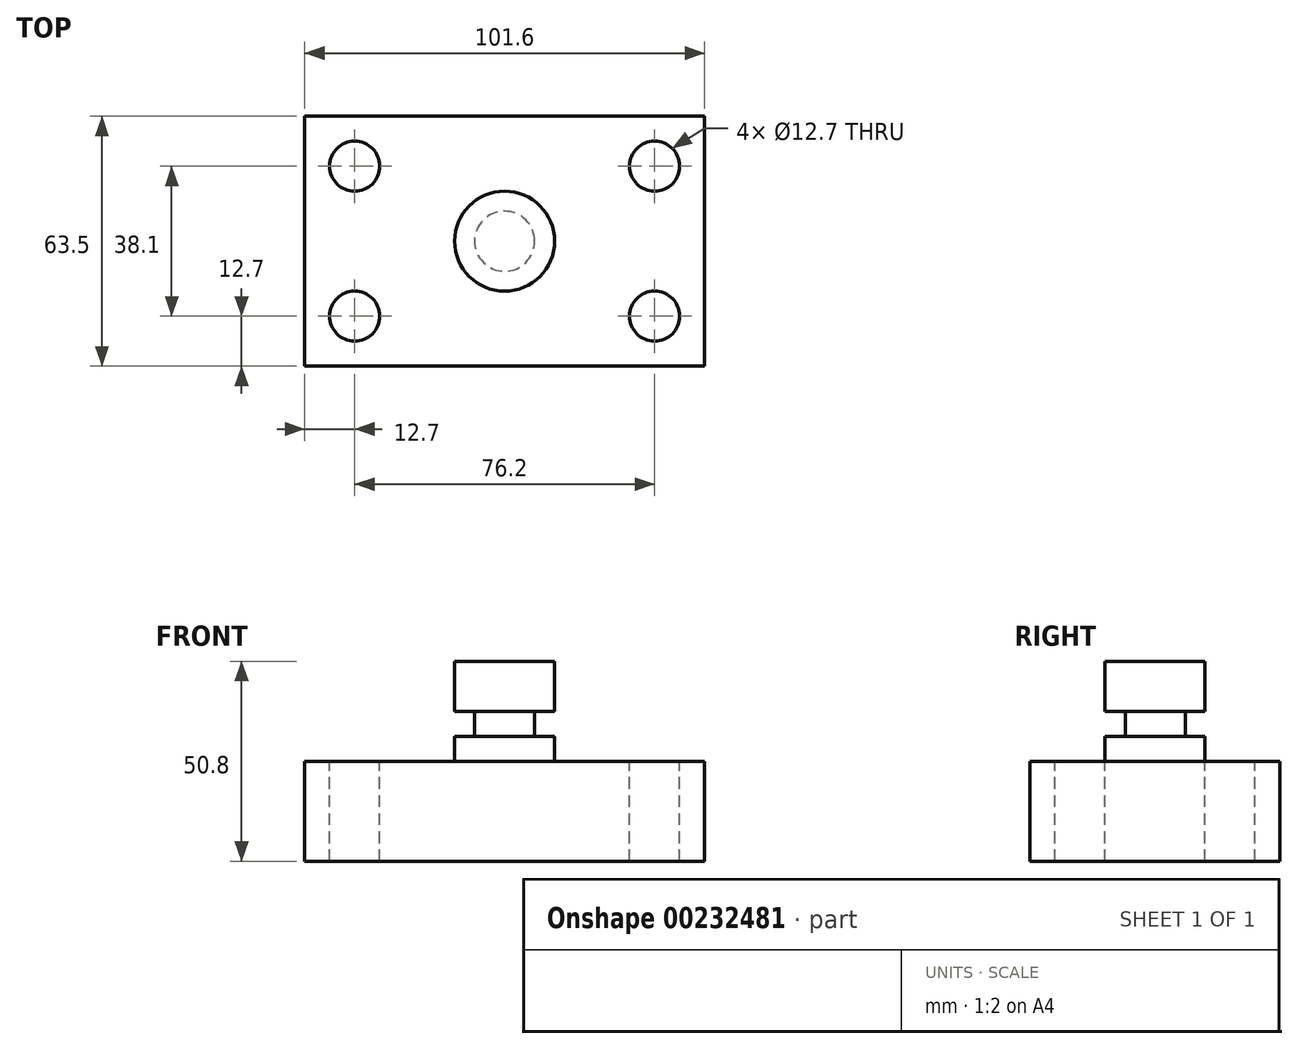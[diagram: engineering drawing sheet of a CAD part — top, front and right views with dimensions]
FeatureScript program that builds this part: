
annotation { "Feature Type Name" : "Feature", "Feature Type Description" : "" }
export const myFeature = defineFeature(function(context is Context, id is Id, definition is map)
    precondition{}
    {
        {
            var Q0;
            Q0=qCreatedBy(makeId("Top.planeOp"),FACE);
            var sketch = newSketch(context, id + "F0", { "sketchPlane" : qUnion([Q0])});
            skLineSegment(sketch, "E0.bottom", {"start": v(-50.8, 31.75) * mm, "end": v(50.8, 31.75) * mm});
            skLineSegment(sketch, "E0.top", {"start": v(-50.8, -31.75) * mm, "end": v(50.8, -31.75) * mm});
            skLineSegment(sketch, "E0.left", {"start": v(-50.8, 31.75) * mm, "end": v(-50.8, -31.75) * mm});
            skLineSegment(sketch, "E0.right", {"start": v(50.8, 31.75) * mm, "end": v(50.8, -31.75) * mm});
            skPoint(sketch, "E0.middle", {"position": v(0, 0) * mm});
            skSolve(sketch);
        }
        {
            var Q0;
            Q0=makeQuery(id+"F0.imprint","IMPRINT",FACE,{"disambiguationData":[TD([[makeQuery(id+"F0.imprint","IMPRINT",EDGE,{"derivedFrom":sQuery(id+"F0.wireOp",EDGE,"E0.bottom")}),-1.0]])]});
            extrude(context, id + "F1", {"entities" : qUnion([Q0]), "flatOperationType" : FlatOperationType.REMOVE, "offsetDistance" : 25.4 * mm, "depth" : 25.4 * mm, "domain" : OperationDomain.MODEL});
        }
        {
            var Q0;
            Q0=makeQuery(id+"F1.opExtrude","CAP_FACE",FACE,{"disambiguationData":[OSD([sQuery(id+"F0.wireOp",EDGE,"E0.bottom"),sQuery(id+"F0.wireOp",EDGE,"E0.top"),sQuery(id+"F0.wireOp",EDGE,"E0.left"),sQuery(id+"F0.wireOp",EDGE,"E0.right")])],"isStart":false});
            var sketch = newSketch(context, id + "F2", { "sketchPlane" : qUnion([Q0])});
            skCircle(sketch, "E1", {"center": v(-38.1, 19.05) * mm, "radius": 6.35 * mm});
            skCircle(sketch, "E2", {"center": v(38.1, 19.05) * mm, "radius": 6.35 * mm});
            skCircle(sketch, "E3", {"center": v(38.1, -19.05) * mm, "radius": 6.35 * mm});
            skCircle(sketch, "E4", {"center": v(-38.1, -19.05) * mm, "radius": 6.35 * mm});
            skSolve(sketch);
        }
        {
            var Q0;
            Q0 = qSketchRegion(id + "F2", true);
            extrude(context, id + "F3", {"entities" : qUnion([Q0]), "operationType" : NewBodyOperationType.REMOVE, "flatOperationType" : FlatOperationType.REMOVE, "endBound" : BoundingType.THROUGH_ALL, "oppositeDirection" : true, "offsetDistance" : 25.4 * mm, "depth" : 25.4 * mm, "domain" : OperationDomain.MODEL});
        }
        {
            var Q0;
            Q0=qCreatedBy(makeId("Front.planeOp"),FACE);
            var sketch = newSketch(context, id + "F4", { "sketchPlane" : qUnion([Q0])});
            skLineSegment(sketch, "E5.bottom", {"start": v(0, 25.4) * mm, "end": v(-12.7, 25.4) * mm});
            skLineSegment(sketch, "E5.top", {"start": v(0, 50.8) * mm, "end": v(-12.7, 50.8) * mm});
            skLineSegment(sketch, "E5.left", {"start": v(0, 25.4) * mm, "end": v(0, 50.8) * mm});
            skLineSegment(sketch, "E5.right", {"start": v(-12.7, 25.4) * mm, "end": v(-12.7, 50.8) * mm});
            skSolve(sketch);
        }
        {
            var Q0;
            Q0=makeQuery(id+"F4.imprint","IMPRINT",FACE,{"disambiguationData":[TD([[makeQuery(id+"F4.imprint","IMPRINT",EDGE,{"derivedFrom":sQuery(id+"F4.wireOp",EDGE,"E5.bottom")}),-1.0]])]});
            var Q1;
            Q1=sQuery(id+"F4.wireOp",EDGE,"E5.left");
            revolve(context, id + "F5", {"operationType" : NewBodyOperationType.ADD, "surfaceOperationType" : NewSurfaceOperationType.NEW, "entities" : qUnion([Q0]), "axis" : qUnion([Q1]), "revolveType" : RevolveType.FULL});
        }
        {
            var Q0;
            Q0=qCreatedBy(makeId("Front.planeOp"),FACE);
            var sketch = newSketch(context, id + "F6", { "sketchPlane" : qUnion([Q0])});
            skLineSegment(sketch, "E6.bottom", {"start": v(-21.24, 38.1) * mm, "end": v(-7.62, 38.1) * mm});
            skLineSegment(sketch, "E6.top", {"start": v(-21.24, 31.75) * mm, "end": v(-7.62, 31.75) * mm});
            skLineSegment(sketch, "E6.left", {"start": v(-21.24, 38.1) * mm, "end": v(-21.24, 31.75) * mm});
            skLineSegment(sketch, "E6.right", {"start": v(-7.62, 38.1) * mm, "end": v(-7.62, 31.75) * mm});
            skSolve(sketch);
        }
        {
            var Q0;
            Q0=makeQuery(id+"F6.imprint","IMPRINT",FACE,{"disambiguationData":[TD([[makeQuery(id+"F6.imprint","IMPRINT",EDGE,{"derivedFrom":sQuery(id+"F6.wireOp",EDGE,"E6.bottom")}),-1.0]])]});
            var Q1;
            Q1=makeQuery(id+"F5.opRevolve","SWEPT_EDGE",EDGE,{"disambiguationData":[OSD([sQuery(id+"F4.wireOp",EDGE,"E5.top"),sQuery(id+"F4.wireOp",EDGE,"E5.right")])]});
            revolve(context, id + "F7", {"operationType" : NewBodyOperationType.REMOVE, "surfaceOperationType" : NewSurfaceOperationType.NEW, "entities" : qUnion([Q0]), "axis" : qUnion([Q1]), "revolveType" : RevolveType.FULL, "oppositeDirection" : true});
        }
    });
